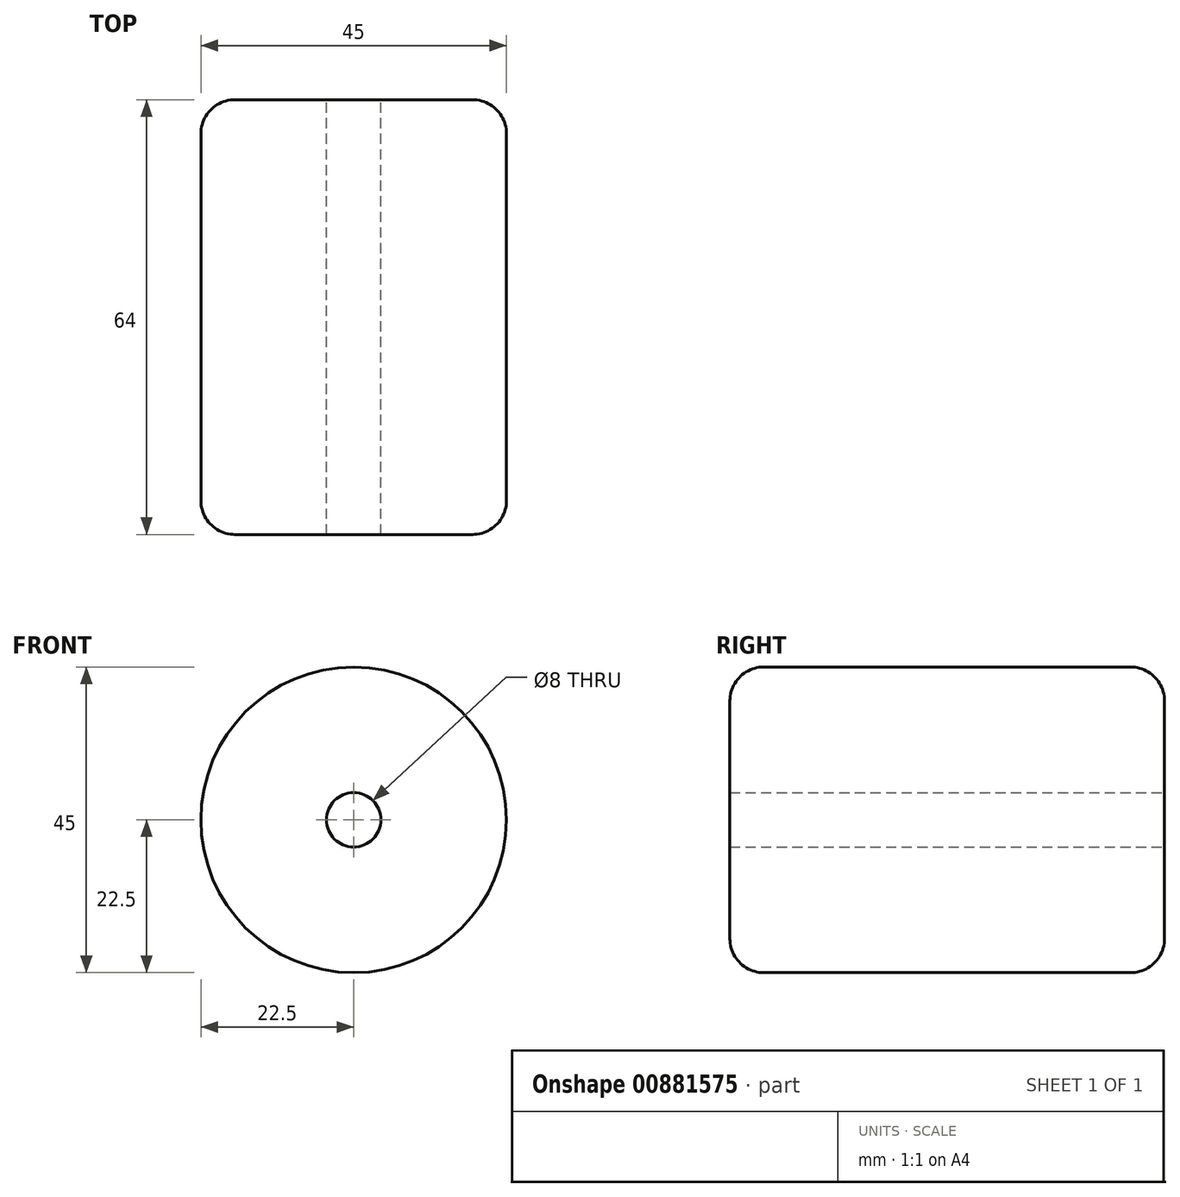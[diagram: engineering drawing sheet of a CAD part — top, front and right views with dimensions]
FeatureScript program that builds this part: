
annotation { "Feature Type Name" : "Feature", "Feature Type Description" : "" }
export const myFeature = defineFeature(function(context is Context, id is Id, definition is map)
    precondition{}
    {
        {
            var Q0;
            Q0=qCreatedBy(makeId("Front.planeOp"),FACE);
            var sketch = newSketch(context, id + "F0", { "sketchPlane" : qUnion([Q0])});
            skCircle(sketch, "E0", {"center": v(0, 0) * mm, "radius": 22.5 * mm});
            skSolve(sketch);
        }
        {
            var Q0;
            Q0 = qSketchRegion(id + "F0", true);
            extrude(context, id + "F1", {"entities" : qUnion([Q0]), "depth" : 64 * mm, "offsetDistance" : 25 * mm});
        }
        {
            var Q0;
            Q0=makeQuery(id+"F1.opExtrude","CAP_FACE",FACE,{"disambiguationData":[OSD([sQuery(id+"F0.wireOp",EDGE,"E0")])],"isStart":true});
            var sketch = newSketch(context, id + "F2", { "sketchPlane" : qUnion([Q0])});
            skCircle(sketch, "E1", {"center": v(0, 0) * mm, "radius": 4 * mm});
            skSolve(sketch);
        }
        {
            var Q0;
            Q0 = qSketchRegion(id + "F2", true);
            extrude(context, id + "F3", {"entities" : qUnion([Q0]), "operationType" : NewBodyOperationType.REMOVE, "oppositeDirection" : true, "depth" : 64 * mm, "offsetDistance" : 25 * mm});
        }
        {
            var Q0;
            Q0=makeQuery(id+"F1.opExtrude","CAP_EDGE",EDGE,{"disambiguationData":[OSD([sQuery(id+"F0.wireOp",EDGE,"E0")])],"isStart":false});
            var Q1;
            Q1=makeQuery(id+"F1.opExtrude","CAP_EDGE",EDGE,{"disambiguationData":[OSD([sQuery(id+"F0.wireOp",EDGE,"E0")])],"isStart":true});
            fillet(context, id + "F4", {"entities" : qUnion([Q0, Q1]), "radius" : 5 * mm, "tangentPropagation" : true, "allowEdgeOverflow" : false});
        }
    });
